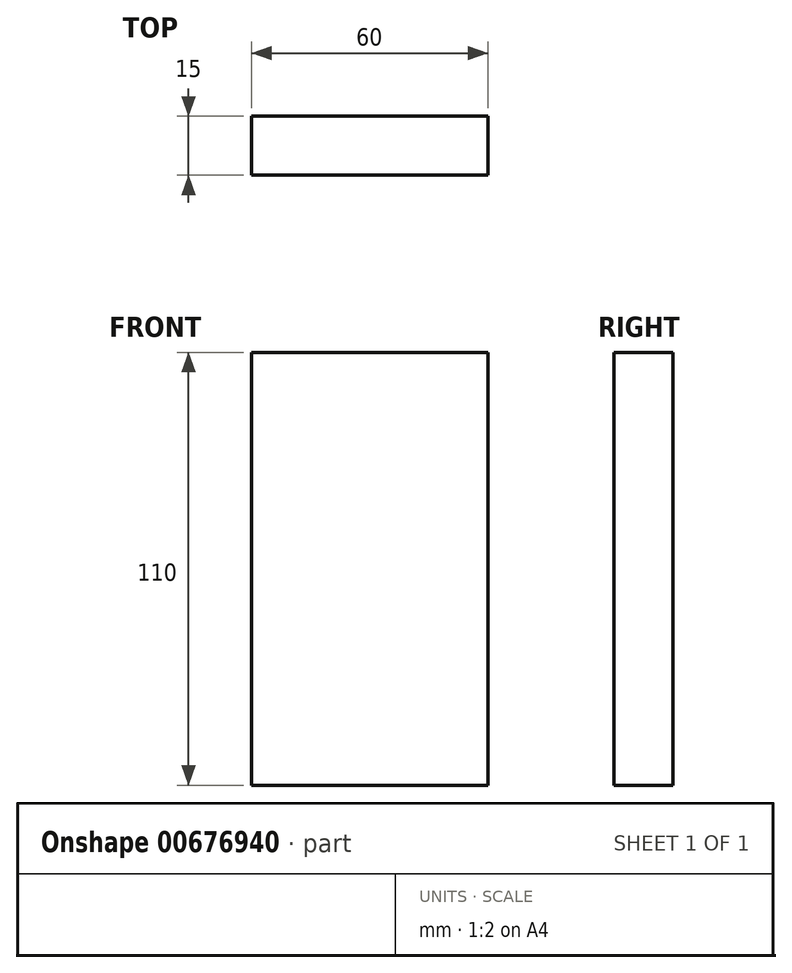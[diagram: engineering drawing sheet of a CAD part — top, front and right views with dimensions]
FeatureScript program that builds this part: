
annotation { "Feature Type Name" : "Feature", "Feature Type Description" : "" }
export const myFeature = defineFeature(function(context is Context, id is Id, definition is map)
    precondition{}
    {
        {
            var Q0;
            Q0=qCreatedBy(makeId("Top.planeOp"),FACE);
            var sketch = newSketch(context, id + "F0", { "sketchPlane" : qUnion([Q0])});
            skLineSegment(sketch, "E0.bottom", {"start": v(30, -7.5) * mm, "end": v(-30, -7.5) * mm});
            skLineSegment(sketch, "E0.top", {"start": v(30, 7.5) * mm, "end": v(-30, 7.5) * mm});
            skLineSegment(sketch, "E0.left", {"start": v(30, -7.5) * mm, "end": v(30, 7.5) * mm});
            skLineSegment(sketch, "E0.right", {"start": v(-30, -7.5) * mm, "end": v(-30, 7.5) * mm});
            skPoint(sketch, "E0.middle", {"position": v(0, 0) * mm});
            skSolve(sketch);
        }
        {
            var Q0;
            Q0=makeQuery(id+"F0.imprint","IMPRINT",FACE,{"disambiguationData":[TD([[makeQuery(id+"F0.imprint","IMPRINT",EDGE,{"derivedFrom":sQuery(id+"F0.wireOp",EDGE,"E0.bottom")}),-1.0]])]});
            var Q1;
            Q1 = qSketchRegion(id + "F2", true);
            extrude(context, id + "F1", {"entities" : qUnion([Q0, Q1]), "depth" : 110 * mm, "offsetDistance" : 25 * mm});
        }
    });
